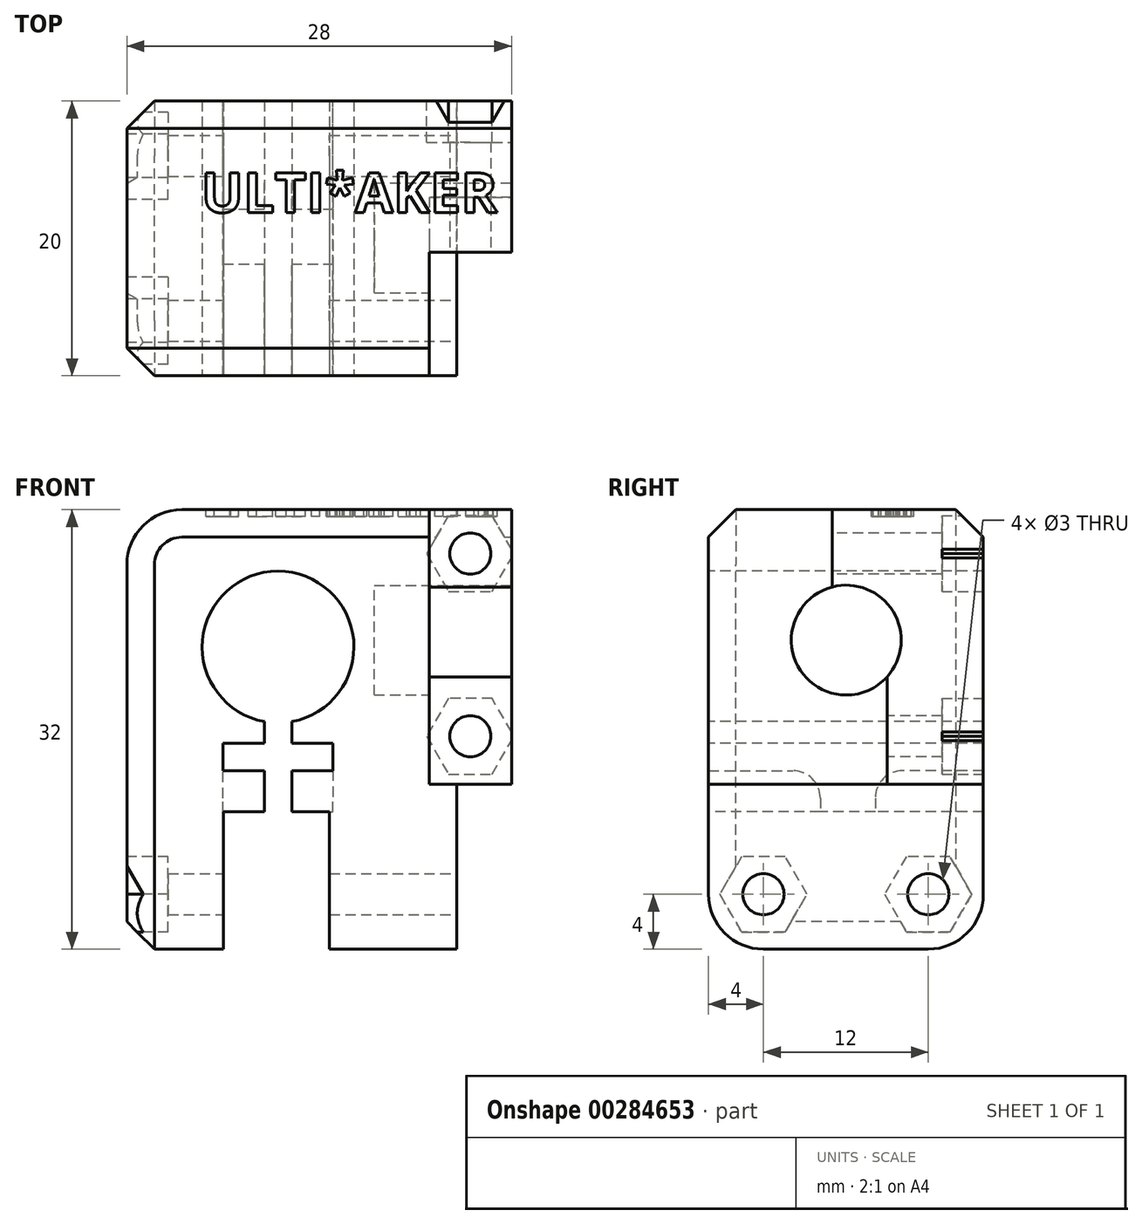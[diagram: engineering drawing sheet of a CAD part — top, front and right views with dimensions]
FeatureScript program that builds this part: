
annotation { "Feature Type Name" : "Feature", "Feature Type Description" : "" }
export const myFeature = defineFeature(function(context is Context, id is Id, definition is map)
    precondition{}
    {
        {
            var Q0;
            Q0=qCreatedBy(makeId("Front.planeOp"),FACE);
            var sketch = newSketch(context, id + "F0", { "sketchPlane" : qUnion([Q0])});
            skLineSegment(sketch, "E0.bottom", {"start": v(0, 0) * mm, "end": v(24, 0) * mm});
            skLineSegment(sketch, "E0.top", {"start": v(0, 32) * mm, "end": v(24, 32) * mm});
            skLineSegment(sketch, "E0.left", {"start": v(0, 0) * mm, "end": v(0, 32) * mm});
            skLineSegment(sketch, "E0.right", {"start": v(24, 0) * mm, "end": v(24, 32) * mm});
            skSolve(sketch);
        }
        {
            var Q0;
            Q0=makeQuery(id+"F0.imprint","IMPRINT",FACE,{"disambiguationData":[TD([[makeQuery(id+"F0.imprint","IMPRINT",EDGE,{"derivedFrom":sQuery(id+"F0.wireOp",EDGE,"E0.bottom")}),1.0]])]});
            extrude(context, id + "F1", {"entities" : qUnion([Q0]), "depth" : 20 * mm});
        }
        {
            var Q0;
            Q0=makeQuery(id+"F1.opExtrude","CAP_FACE",FACE,{"disambiguationData":[OSD([sQuery(id+"F0.wireOp",EDGE,"E0.bottom"),sQuery(id+"F0.wireOp",EDGE,"E0.top"),sQuery(id+"F0.wireOp",EDGE,"E0.left"),sQuery(id+"F0.wireOp",EDGE,"E0.right")])],"isStart":false});
            var sketch = newSketch(context, id + "F2", { "sketchPlane" : qUnion([Q0])});
            skLineSegment(sketch, "E1.bottom", {"start": v(24, 32) * mm, "end": v(22, 32) * mm});
            skLineSegment(sketch, "E1.top", {"start": v(24, 12) * mm, "end": v(22, 12) * mm});
            skLineSegment(sketch, "E1.left", {"start": v(24, 32) * mm, "end": v(24, 12) * mm});
            skLineSegment(sketch, "E1.right", {"start": v(22, 32) * mm, "end": v(22, 12) * mm});
            skSolve(sketch);
        }
        {
            var Q0;
            Q0 = qSketchRegion(id + "F2", true);
            extrude(context, id + "F3", {"entities" : qUnion([Q0]), "operationType" : NewBodyOperationType.REMOVE, "oppositeDirection" : true, "depth" : 9 * mm});
        }
        {
            var Q0;
            Q0=makeQuery(id+"F1.opExtrude","CAP_FACE",FACE,{"disambiguationData":[OSD([sQuery(id+"F0.wireOp",EDGE,"E0.bottom"),sQuery(id+"F0.wireOp",EDGE,"E0.top"),sQuery(id+"F0.wireOp",EDGE,"E0.left"),sQuery(id+"F0.wireOp",EDGE,"E0.right")])],"isStart":false});
            var sketch = newSketch(context, id + "F4", { "sketchPlane" : qUnion([Q0])});
            skCircle(sketch, "E2", {"center": v(11, 22) * mm, "radius": 5.53 * mm});
            skPoint(sketch, "E2.centerSnap0", {"position": v(11, 32) * mm});
            skSolve(sketch);
        }
        {
            var Q0;
            Q0 = qSketchRegion(id + "F4", true);
            extrude(context, id + "F5", {"entities" : qUnion([Q0]), "operationType" : NewBodyOperationType.REMOVE, "oppositeDirection" : true, "depth" : 25 * mm});
        }
        {
            var Q0;
            Q0=makeQuery(id+"F1.opExtrude","CAP_FACE",FACE,{"disambiguationData":[OSD([sQuery(id+"F0.wireOp",EDGE,"E0.bottom"),sQuery(id+"F0.wireOp",EDGE,"E0.top"),sQuery(id+"F0.wireOp",EDGE,"E0.left"),sQuery(id+"F0.wireOp",EDGE,"E0.right")])],"isStart":false});
            var sketch = newSketch(context, id + "F6", { "sketchPlane" : qUnion([Q0])});
            skLineSegment(sketch, "E3.bottom", {"start": v(10, 20.17) * mm, "end": v(12, 20.17) * mm});
            skLineSegment(sketch, "E3.top", {"start": v(10, -0.17) * mm, "end": v(12, -0.17) * mm});
            skLineSegment(sketch, "E3.left", {"start": v(10, 20.17) * mm, "end": v(10, 10) * mm});
            skLineSegment(sketch, "E3.right", {"start": v(12, 20.17) * mm, "end": v(12, 10) * mm});
            skPoint(sketch, "E4.firstSnap0", {"position": v(10, 10) * mm});
            skLineSegment(sketch, "E4.bottom", {"start": v(14.75, 10) * mm, "end": v(12, 10) * mm});
            skLineSegment(sketch, "E4.top", {"start": v(14.75, -0.17) * mm, "end": v(12, -0.17) * mm});
            skLineSegment(sketch, "E4.left", {"start": v(14.75, 10) * mm, "end": v(14.75, -0.17) * mm});
            skLineSegment(sketch, "E4.right", {"start": v(7.01, 10) * mm, "end": v(7.01, -0.17) * mm});
            skLineSegment(sketch, "E5", {"start": v(11, 0.9) * mm, "end": v(11, 22) * mm, "construction": true});
            skPoint(sketch, "E5.startSnap0", {"position": v(11, 20.17) * mm});
            skLineSegment(sketch, "E6.trimOffspring", {"start": v(10, 10) * mm, "end": v(7.01, 10) * mm});
            skLineSegment(sketch, "E7.trimOffspring", {"start": v(10, -0.17) * mm, "end": v(7.01, -0.17) * mm});
            skSolve(sketch);
        }
        {
            var Q0;
            Q0 = qSketchRegion(id + "F6", true);
            extrude(context, id + "F7", {"entities" : qUnion([Q0]), "operationType" : NewBodyOperationType.REMOVE, "oppositeDirection" : true, "depth" : 25 * mm});
        }
        {
            var Q0;
            Q0=makeQuery(id+"F1.opExtrude","SWEPT_FACE",FACE,{"disambiguationData":[OSD([sQuery(id+"F0.wireOp",EDGE,"E0.right")])]});
            var sketch = newSketch(context, id + "F8", { "sketchPlane" : qUnion([Q0])});
            skCircle(sketch, "E8", {"center": v(-16, 4) * mm, "radius": 1.5 * mm});
            skCircle(sketch, "E9", {"center": v(-4, 4) * mm, "radius": 1.5 * mm});
            skSolve(sketch);
        }
        {
            var Q0;
            Q0 = qSketchRegion(id + "F8", true);
            extrude(context, id + "F9", {"entities" : qUnion([Q0]), "operationType" : NewBodyOperationType.REMOVE, "oppositeDirection" : true, "depth" : 25 * mm});
        }
        {
            var Q0;
            Q0=makeQuery(id+"F1.opExtrude","SWEPT_FACE",FACE,{"disambiguationData":[OSD([sQuery(id+"F0.wireOp",EDGE,"E0.right")])]});
            var sketch = newSketch(context, id + "F10", { "sketchPlane" : qUnion([Q0])});
            skCircle(sketch, "E10", {"center": v(-9.97, 22.5) * mm, "radius": 4 * mm});
            skLineSegment(sketch, "E11", {"start": v(-10, 0) * mm, "end": v(-9.97, 22.5) * mm, "construction": true});
            skSolve(sketch);
        }
        {
            var Q0;
            {var subQ0=sQuery(id+"F10.wireOp",EDGE,"E10");var subQ1=makeQuery(id+"F3.boolean.opBoolean","COPY",EDGE,{"derivedFrom":makeQuery(id+"F3.opExtrude","CAP_EDGE",EDGE,{"disambiguationData":[OSD([sQuery(id+"F2.wireOp",EDGE,"E1.left")])],"isStart":false})});var subQ2=makeQuery(id+"F10.imprint","INTERSECT",VERTEX,{"disambiguationData":[OD(0.0)],"derivedFrom":[subQ1,subQ0]});Q0=makeQuery(id+"F10.imprint","IMPRINT",FACE,{"disambiguationData":[TD([[makeQuery(id+"F10.imprint","IMPRINT",EDGE,{"disambiguationData":[TD([[subQ2,-1.0]])],"derivedFrom":subQ0}),1.0]])]});}
            var Q1;
            {var subQ0=sQuery(id+"F10.wireOp",EDGE,"E10");var subQ1=makeQuery(id+"F3.boolean.opBoolean","COPY",EDGE,{"derivedFrom":makeQuery(id+"F3.opExtrude","CAP_EDGE",EDGE,{"disambiguationData":[OSD([sQuery(id+"F2.wireOp",EDGE,"E1.left")])],"isStart":false})});var subQ2=makeQuery(id+"F10.imprint","INTERSECT",VERTEX,{"disambiguationData":[OD(0.0)],"derivedFrom":[subQ1,subQ0]});Q1=makeQuery(id+"F10.imprint","IMPRINT",FACE,{"disambiguationData":[TD([[makeQuery(id+"F10.imprint","IMPRINT",EDGE,{"disambiguationData":[TD([[subQ2,1.0]])],"derivedFrom":subQ0}),1.0]])]});}
            var Q2;
            Q2=sQuery(id+"F10.wireOp",EDGE,"E10");
            extrude(context, id + "F11", {"entities" : qUnion([Q0, Q1]), "operationType" : NewBodyOperationType.REMOVE, "surfaceEntities" : qUnion([Q2]), "oppositeDirection" : true, "depth" : 6 * mm});
        }
        {
            var Q0;
            Q0=makeQuery(id+"F3.boolean.opBoolean","COPY",FACE,{"derivedFrom":makeQuery(id+"F3.opExtrude","SWEPT_FACE",FACE,{"disambiguationData":[OSD([sQuery(id+"F2.wireOp",EDGE,"E1.right")])]})});
            var sketch = newSketch(context, id + "F12", { "sketchPlane" : qUnion([Q0])});
            skLineSegment(sketch, "E12.bottom", {"start": v(-20, 12) * mm, "end": v(-7, 12) * mm});
            skLineSegment(sketch, "E12.top", {"start": v(-20, 20.42) * mm, "end": v(-7, 20.42) * mm});
            skLineSegment(sketch, "E12.left", {"start": v(-20, 12) * mm, "end": v(-20, 20.42) * mm});
            skLineSegment(sketch, "E12.right", {"start": v(-7, 12) * mm, "end": v(-7, 20.42) * mm});
            skSolve(sketch);
        }
        {
            var Q0;
            Q0 = qSketchRegion(id + "F12", true);
            extrude(context, id + "F13", {"entities" : qUnion([Q0]), "operationType" : NewBodyOperationType.REMOVE, "depth" : 25 * mm});
        }
        {
            var Q0;
            Q0=makeQuery(id+"F1.opExtrude","SWEPT_FACE",FACE,{"disambiguationData":[OSD([sQuery(id+"F0.wireOp",EDGE,"E0.right")])]});
            var sketch = newSketch(context, id + "F14", { "sketchPlane" : qUnion([Q0])});
            skLineSegment(sketch, "E13.bottom", {"start": v(-7, 12) * mm, "end": v(0, 12) * mm});
            skLineSegment(sketch, "E13.top", {"start": v(-7, 32) * mm, "end": v(0, 32) * mm});
            skLineSegment(sketch, "E13.left", {"start": v(-7, 12) * mm, "end": v(-7, 19.82) * mm});
            skLineSegment(sketch, "E13.right", {"start": v(0, 12) * mm, "end": v(0, 32) * mm});
            skLineSegment(sketch, "E14.bottom", {"start": v(-11, 32) * mm, "end": v(0, 32) * mm});
            skLineSegment(sketch, "E14.left", {"start": v(-11, 32) * mm, "end": v(-11, 26.37) * mm});
            skLineSegment(sketch, "E14.right", {"start": v(0, 32) * mm, "end": v(0, 23.43) * mm});
            skArc(sketch, "E15", {"start": v(-7, 19.82) * mm, "mid": v(-6.56, 24.59) * mm, "end": v(-11, 26.37) * mm});
            skSolve(sketch);
        }
        {
            var Q0;
            Q0 = qSketchRegion(id + "F14", true);
            extrude(context, id + "F15", {"entities" : qUnion([Q0]), "operationType" : NewBodyOperationType.ADD, "depth" : 4 * mm});
        }
        {
            var Q0;
            Q0=makeQuery(id+"F15.boolean.opBoolean","MERGE",FACE,{"derivedFrom":[makeQuery(id+"F13.boolean.opBoolean","COPY",FACE,{"derivedFrom":makeQuery(id+"F13.opExtrude","SWEPT_FACE",FACE,{"disambiguationData":[OSD([sQuery(id+"F12.wireOp",EDGE,"E12.right")])]})}),makeQuery(id+"F15.opExtrude","SWEPT_FACE",FACE,{"disambiguationData":[OSD([sQuery(id+"F14.wireOp",EDGE,"E13.left")])]})]});
            var sketch = newSketch(context, id + "F16", { "sketchPlane" : qUnion([Q0])});
            skCircle(sketch, "E16", {"center": v(25, 15.5) * mm, "radius": 1.5 * mm});
            skPoint(sketch, "E16.centerSnap0", {"position": v(28, 15.5) * mm});
            skPoint(sketch, "E16.centerSnap1", {"position": v(25, 19.82) * mm});
            skCircle(sketch, "E17", {"center": v(25, 28.8) * mm, "radius": 1.5 * mm});
            skSolve(sketch);
        }
        {
            var Q0;
            Q0 = qSketchRegion(id + "F16", true);
            extrude(context, id + "F17", {"entities" : qUnion([Q0]), "operationType" : NewBodyOperationType.REMOVE, "endBound" : BoundingType.SYMMETRIC, "oppositeDirection" : true, "depth" : 25 * mm});
        }
        {
            var Q0;
            Q0=makeQuery(id+"F15.boolean.opBoolean","MERGE",FACE,{"derivedFrom":[makeQuery(id+"F1.opExtrude","CAP_FACE",FACE,{"disambiguationData":[OSD([sQuery(id+"F0.wireOp",EDGE,"E0.bottom"),sQuery(id+"F0.wireOp",EDGE,"E0.top"),sQuery(id+"F0.wireOp",EDGE,"E0.left"),sQuery(id+"F0.wireOp",EDGE,"E0.right")])],"isStart":true}),makeQuery(id+"F15.opExtrude","SWEPT_FACE",FACE,{"disambiguationData":[OSD([sQuery(id+"F14.wireOp",EDGE,"E13.right"),sQuery(id+"F14.wireOp",EDGE,"E14.right")])]})]});
            var sketch = newSketch(context, id + "F18", { "sketchPlane" : qUnion([Q0])});
            skCircle(sketch, "E18.cCircle", {"center": v(-25, 28.8) * mm, "radius": 2.75 * mm, "construction": true});
            skLineSegment(sketch, "E18.0", {"start": v(-26.59, 26.05) * mm, "end": v(-28.18, 28.8) * mm});
            skLineSegment(sketch, "E18.1", {"start": v(-28.18, 28.8) * mm, "end": v(-26.59, 31.55) * mm});
            skLineSegment(sketch, "E18.2", {"start": v(-26.59, 31.55) * mm, "end": v(-23.41, 31.55) * mm});
            skLineSegment(sketch, "E18.3", {"start": v(-23.41, 31.55) * mm, "end": v(-21.82, 28.8) * mm});
            skLineSegment(sketch, "E18.4", {"start": v(-21.82, 28.8) * mm, "end": v(-23.41, 26.05) * mm});
            skLineSegment(sketch, "E18.5", {"start": v(-23.41, 26.05) * mm, "end": v(-26.59, 26.05) * mm});
            skPoint(sketch, "E18.0.midPoint", {"position": v(-27.38, 27.42) * mm});
            skCircle(sketch, "E19.cCircle", {"center": v(-25, 15.5) * mm, "radius": 2.75 * mm, "construction": true});
            skLineSegment(sketch, "E19.0", {"start": v(-28.18, 15.5) * mm, "end": v(-26.59, 18.25) * mm});
            skLineSegment(sketch, "E19.1", {"start": v(-26.59, 18.25) * mm, "end": v(-23.41, 18.25) * mm});
            skLineSegment(sketch, "E19.2", {"start": v(-23.41, 18.25) * mm, "end": v(-21.82, 15.5) * mm});
            skLineSegment(sketch, "E19.3", {"start": v(-21.82, 15.5) * mm, "end": v(-23.41, 12.75) * mm});
            skLineSegment(sketch, "E19.4", {"start": v(-23.41, 12.75) * mm, "end": v(-26.59, 12.75) * mm});
            skLineSegment(sketch, "E19.5", {"start": v(-26.59, 12.75) * mm, "end": v(-28.18, 15.5) * mm});
            skPoint(sketch, "E19.0.midPoint", {"position": v(-27.38, 16.87) * mm});
            skSolve(sketch);
        }
        {
            var Q0;
            Q0 = qSketchRegion(id + "F18", true);
            extrude(context, id + "F19", {"entities" : qUnion([Q0]), "operationType" : NewBodyOperationType.REMOVE, "oppositeDirection" : true, "depth" : 3 * mm});
        }
        {
            var Q0;
            Q0=makeQuery(id+"F1.opExtrude","SWEPT_FACE",FACE,{"disambiguationData":[OSD([sQuery(id+"F0.wireOp",EDGE,"E0.left")])]});
            var sketch = newSketch(context, id + "F20", { "sketchPlane" : qUnion([Q0])});
            skCircle(sketch, "E20.cCircle", {"center": v(4, 4) * mm, "radius": 2.75 * mm, "construction": true});
            skLineSegment(sketch, "E20.0", {"start": v(2.41, 6.75) * mm, "end": v(5.59, 6.75) * mm});
            skLineSegment(sketch, "E20.1", {"start": v(5.59, 6.75) * mm, "end": v(7.18, 4) * mm});
            skLineSegment(sketch, "E20.2", {"start": v(7.18, 4) * mm, "end": v(5.59, 1.25) * mm});
            skLineSegment(sketch, "E20.3", {"start": v(5.59, 1.25) * mm, "end": v(2.41, 1.25) * mm});
            skLineSegment(sketch, "E20.4", {"start": v(2.41, 1.25) * mm, "end": v(0.82, 4) * mm});
            skLineSegment(sketch, "E20.5", {"start": v(0.82, 4) * mm, "end": v(2.41, 6.75) * mm});
            skPoint(sketch, "E20.0.midPoint", {"position": v(4, 6.75) * mm});
            skCircle(sketch, "E21.cCircle", {"center": v(16, 4) * mm, "radius": 2.75 * mm, "construction": true});
            skLineSegment(sketch, "E21.0", {"start": v(14.41, 6.75) * mm, "end": v(17.59, 6.75) * mm});
            skLineSegment(sketch, "E21.1", {"start": v(17.59, 6.75) * mm, "end": v(19.18, 4) * mm});
            skLineSegment(sketch, "E21.2", {"start": v(19.18, 4) * mm, "end": v(17.59, 1.25) * mm});
            skLineSegment(sketch, "E21.3", {"start": v(17.59, 1.25) * mm, "end": v(14.41, 1.25) * mm});
            skLineSegment(sketch, "E21.4", {"start": v(14.41, 1.25) * mm, "end": v(12.82, 4) * mm});
            skLineSegment(sketch, "E21.5", {"start": v(12.82, 4) * mm, "end": v(14.41, 6.75) * mm});
            skPoint(sketch, "E21.0.midPoint", {"position": v(16, 6.75) * mm});
            skSolve(sketch);
        }
        {
            var Q0;
            Q0 = qSketchRegion(id + "F20", true);
            extrude(context, id + "F21", {"entities" : qUnion([Q0]), "operationType" : NewBodyOperationType.REMOVE, "oppositeDirection" : true, "depth" : 3 * mm});
        }
        {
            var Q0;
            Q0=makeQuery(id+"F1.opExtrude","SWEPT_EDGE",EDGE,{"disambiguationData":[OSD([sQuery(id+"F0.wireOp",EDGE,"E0.top"),sQuery(id+"F0.wireOp",EDGE,"E0.left")])]});
            var Q1;
            {var subQ0=sQuery(id+"F0.wireOp",EDGE,"E0.bottom");var subQ1=sQuery(id+"F0.wireOp",EDGE,"E0.left");Q1=makeQuery(id+"F7.boolean.opBoolean","SPLIT",EDGE,{"disambiguationData":[TD([makeQuery(id+"F1.opExtrude","SWEPT_FACE",FACE,{"disambiguationData":[OSD([subQ1])]})])],"derivedFrom":makeQuery(id+"F1.opExtrude","CAP_EDGE",EDGE,{"disambiguationData":[OSD([subQ0])],"isStart":false})});}
            var Q2;
            {var subQ0=sQuery(id+"F0.wireOp",EDGE,"E0.bottom");var subQ1=sQuery(id+"F0.wireOp",EDGE,"E0.left");Q2=makeQuery(id+"F7.boolean.opBoolean","SPLIT",EDGE,{"disambiguationData":[TD([makeQuery(id+"F1.opExtrude","SWEPT_FACE",FACE,{"disambiguationData":[OSD([subQ1])]})])],"derivedFrom":makeQuery(id+"F1.opExtrude","CAP_EDGE",EDGE,{"disambiguationData":[OSD([subQ0])],"isStart":true})});}
            var Q3;
            {var subQ0=sQuery(id+"F0.wireOp",EDGE,"E0.bottom");var subQ1=sQuery(id+"F0.wireOp",EDGE,"E0.right");Q3=makeQuery(id+"F7.boolean.opBoolean","SPLIT",EDGE,{"disambiguationData":[TD([makeQuery(id+"F1.opExtrude","SWEPT_FACE",FACE,{"disambiguationData":[OSD([subQ1])]})])],"derivedFrom":makeQuery(id+"F1.opExtrude","CAP_EDGE",EDGE,{"disambiguationData":[OSD([subQ0])],"isStart":true})});}
            var Q4;
            {var subQ0=sQuery(id+"F0.wireOp",EDGE,"E0.bottom");var subQ1=sQuery(id+"F0.wireOp",EDGE,"E0.right");Q4=makeQuery(id+"F7.boolean.opBoolean","SPLIT",EDGE,{"disambiguationData":[TD([makeQuery(id+"F1.opExtrude","SWEPT_FACE",FACE,{"disambiguationData":[OSD([subQ1])]})])],"derivedFrom":makeQuery(id+"F1.opExtrude","CAP_EDGE",EDGE,{"disambiguationData":[OSD([subQ0])],"isStart":false})});}
            fillet(context, id + "F22", {"entities" : qUnion([Q0, Q1, Q2, Q3, Q4]), "radius" : 4 * mm, "tangentPropagation" : true, "allowEdgeOverflow" : false});
        }
        {
            var Q0;
            Q0=makeQuery(id+"F1.opExtrude","CAP_EDGE",EDGE,{"disambiguationData":[OSD([sQuery(id+"F0.wireOp",EDGE,"E0.top")])],"isStart":false});
            var Q1;
            {var subQ0=sQuery(id+"F0.wireOp",EDGE,"E0.left");var subQ1=sQuery(id+"F0.wireOp",EDGE,"E0.top");Q1=makeQuery(id+"F22.opFillet","BLEND_EDGE",EDGE,{"blendedFrom":[makeQuery(id+"F1.opExtrude","SWEPT_EDGE",EDGE,{"disambiguationData":[OSD([subQ1,subQ0])]}),makeQuery(id+"F1.opExtrude","CAP_FACE",FACE,{"disambiguationData":[OSD([sQuery(id+"F0.wireOp",EDGE,"E0.bottom"),subQ1,subQ0,sQuery(id+"F0.wireOp",EDGE,"E0.right")])],"isStart":false})],"blendedInto":[makeQuery(id+"F1.opExtrude","CAP_FACE",FACE,{"disambiguationData":[OSD([sQuery(id+"F0.wireOp",EDGE,"E0.bottom"),subQ1,subQ0,sQuery(id+"F0.wireOp",EDGE,"E0.right")])],"isStart":false})]});}
            chamfer(context, id + "F23", {"entities" : qUnion([Q0, Q1]), "width" : 2 * mm, "tangentPropagation" : true});
        }
        {
            var Q0;
            Q0=makeQuery(id+"F15.boolean.opBoolean","MERGE",FACE,{"derivedFrom":[makeQuery(id+"F1.opExtrude","SWEPT_FACE",FACE,{"disambiguationData":[OSD([sQuery(id+"F0.wireOp",EDGE,"E0.top")])]}),makeQuery(id+"F15.opExtrude","SWEPT_FACE",FACE,{"disambiguationData":[OSD([sQuery(id+"F14.wireOp",EDGE,"E14.bottom")])]})]});
            var sketch = newSketch(context, id + "F24", { "sketchPlane" : qUnion([Q0])});
            skText(sketch, "E22", { "text": "ULTI*AKER", "fontName": "OpenSans-Bold.ttf"});
            const initialGuessF24  = {"E22": [0.00542, -0.00811, 1, 0, 0.0029]};
            skSetInitialGuess(sketch, initialGuessF24);
            skSolve(sketch);
        }
        {
            var Q0;
            Q0 = qSketchRegion(id + "F24", true);
            extrude(context, id + "F25", {"entities" : qUnion([Q0]), "operationType" : NewBodyOperationType.REMOVE, "oppositeDirection" : true, "depth" : 0.5 * mm});
        }
        {
            var Q0;
            Q0=makeQuery(id+"F7.boolean.opBoolean","COPY",FACE,{"derivedFrom":makeQuery(id+"F7.opExtrude","SWEPT_FACE",FACE,{"disambiguationData":[OSD([sQuery(id+"F6.wireOp",EDGE,"E3.left")])]})});
            var sketch = newSketch(context, id + "F26", { "sketchPlane" : qUnion([Q0])});
            skLineSegment(sketch, "E23.bottom", {"start": v(-11.86, 10) * mm, "end": v(-7.86, 10) * mm});
            skLineSegment(sketch, "E23.top", {"start": v(-11.86, 15) * mm, "end": v(-7.86, 15) * mm});
            skLineSegment(sketch, "E23.left", {"start": v(-11.86, 10) * mm, "end": v(-11.86, 11) * mm});
            skLineSegment(sketch, "E23.right", {"start": v(-7.86, 10) * mm, "end": v(-7.86, 11) * mm});
            skLineSegment(sketch, "E24.bottom", {"start": v(-11.86, 15) * mm, "end": v(-34.04, 15) * mm});
            skLineSegment(sketch, "E24.top", {"start": v(-13.86, 13) * mm, "end": v(-34.04, 13) * mm});
            skLineSegment(sketch, "E24.right", {"start": v(-34.04, 15) * mm, "end": v(-34.04, 13) * mm});
            skLineSegment(sketch, "E25.bottom", {"start": v(-7.86, 15) * mm, "end": v(14.67, 15) * mm});
            skLineSegment(sketch, "E25.top", {"start": v(-5.86, 13) * mm, "end": v(14.67, 13) * mm});
            skLineSegment(sketch, "E25.right", {"start": v(14.67, 15) * mm, "end": v(14.67, 13) * mm});
            skPoint(sketch, "E26.visualSharp", {"position": v(-11.86, 13) * mm});
            skArc(sketch, "E26.filletArc", {"start": v(-11.86, 11) * mm, "mid": v(-12.45, 12.41) * mm, "end": v(-13.86, 13) * mm});
            skPoint(sketch, "E27.visualSharp", {"position": v(-7.86, 13) * mm});
            skArc(sketch, "E27.filletArc", {"start": v(-5.86, 13) * mm, "mid": v(-7.28, 12.41) * mm, "end": v(-7.86, 11) * mm});
            skSolve(sketch);
        }
        {
            var Q0;
            Q0=makeQuery(id+"F26.imprint","IMPRINT",FACE,{"disambiguationData":[TD([[makeQuery(id+"F26.imprint","IMPRINT",EDGE,{"derivedFrom":sQuery(id+"F26.wireOp",EDGE,"E23.bottom")}),-1.0]])]});
            extrude(context, id + "F27", {"entities" : qUnion([Q0]), "operationType" : NewBodyOperationType.REMOVE, "oppositeDirection" : true, "depth" : 3 * mm, "hasSecondDirection" : true, "secondDirectionOppositeDirection" : false, "secondDirectionDepth" : 5 * mm});
        }
    });
